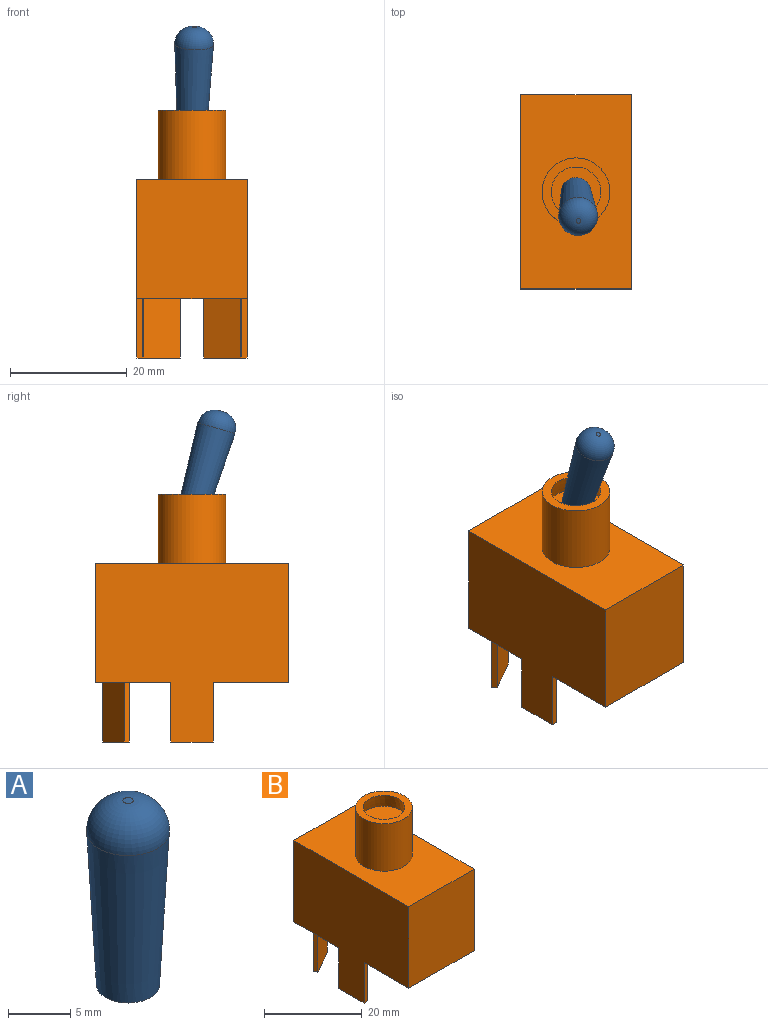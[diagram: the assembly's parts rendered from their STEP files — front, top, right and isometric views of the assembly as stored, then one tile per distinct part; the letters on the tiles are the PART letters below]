
ASSEMBLY  parts=2 mates=1
PART A: 4 faces, bbox 6.7x6.7x18.2 mm
  f0: cone r=2.54mm half-angle=3deg, axis (0,0,1), area 278.6mm2, adj f2,f3
  f1: plane 0.83x0.83mm, normal (0,0,1), area 0.5mm2, adj f3
  f2: plane 5.08x5.08mm, normal (0,0,-1), area 20.3mm2, adj f0
  f3: torus R=0.41mm, axis (0,0,1), area 68.7mm2, adj f0,f1
PART B: 28 faces, bbox 18.9x33.3x42.5 mm
  f0: plane 33.27x18.92mm, normal (0,0,-1), area 599.7mm2, adj f1,f2,f3,f4,f10,f11,f12,f14
  f1: plane 20.45x18.92mm, normal (0,-1,0), area 386.9mm2, adj f0,f2,f4,f5
  f2: plane 33.27x30.61mm, normal (1,0,0), area 755.2mm2, adj f0,f1,f3,f5,f14,f16,f17
  f3: plane 20.45x18.92mm, normal (0,1,0), area 386.9mm2, adj f0,f2,f4,f5
  f4: plane 33.27x30.61mm, normal (-1,0,0), area 755.2mm2, adj f0,f1,f3,f5,f10,f11,f13
  f5: plane 33.27x18.92mm, normal (0,0,1), area 523.4mm2, adj f1,f2,f3,f4,f6
  f6: cylinder r=5.82mm len=11.89mm, axis (0,0,-1), area 434.4mm2, adj f5,f7
  f7: plane 11.63x11.63mm, normal (0,0,1), area 49.4mm2, adj f6,f8
  f8: cone r=4.25mm half-angle=12deg, axis (0,0,-1), area 93.7mm2, adj f7,f9
  f9: plane 9.86x9.86mm, normal (0,0,1), area 76.3mm2, adj f8
  f10: plane 10.16x1.02mm, normal (0,-1,0), area 10.3mm2, adj f0,f4,f12,f13
  f11: plane 10.16x1.02mm, normal (0,1,0), area 10.3mm2, adj f0,f4,f12,f13
  f12: plane 10.16x7.37mm, normal (1,0,0), area 74.8mm2, adj f0,f10,f11,f13
  f13: plane 7.37x1.02mm, normal (0,0,-1), area 7.5mm2, adj f4,f10,f11,f12
  f14: plane 10.16x1.02mm, normal (0,-1,0), area 10.3mm2, adj f0,f2,f15,f17
  f15: plane 10.16x7.37mm, normal (-1,0,0), area 74.8mm2, adj f0,f14,f16,f17
  f16: plane 10.16x1.02mm, normal (0,1,0), area 10.3mm2, adj f0,f2,f15,f17
  f17: plane 7.37x1.02mm, normal (0,0,-1), area 7.5mm2, adj f2,f14,f15,f16
  f18: plane 10.16x0.88mm, normal (-0.87,0.5,0), area 10.3mm2, adj f0,f19,f21,f22
  f19: plane 10.16x6.38mm, normal (0.5,0.87,0), area 74.8mm2, adj f0,f18,f20,f22
  f20: plane 10.16x0.88mm, normal (0.87,-0.5,0), area 10.3mm2, adj f0,f19,f21,f22
  f21: plane 10.16x6.38mm, normal (-0.5,-0.87,0), area 74.8mm2, adj f0,f18,f20,f22
  f22: plane 6.89x4.56mm, normal (0,0,-1), area 7.5mm2, adj f18,f19,f20,f21
  f23: plane 10.16x6.38mm, normal (0.5,-0.87,0), area 74.8mm2, adj f0,f24,f26,f27
  f24: plane 10.16x0.88mm, normal (-0.87,-0.5,0), area 10.3mm2, adj f0,f23,f25,f27
  f25: plane 10.16x6.38mm, normal (-0.5,0.87,0), area 74.8mm2, adj f0,f24,f26,f27
  f26: plane 10.16x0.88mm, normal (0.87,0.5,0), area 10.3mm2, adj f0,f23,f25,f27
  f27: plane 6.89x4.56mm, normal (0,0,-1), area 7.5mm2, adj f23,f24,f25,f26
PLACE A rot(axis=(0.96,0.04,0.28),16.8deg) t=(-0.36,2.45,9.89)mm
PLACE B t=(-0.15,0.04,9.55)mm fixed
MATE ball B.f8 <-> A.f0  axis (0,0,1) through (-0.15,0.04,18.26)mm
